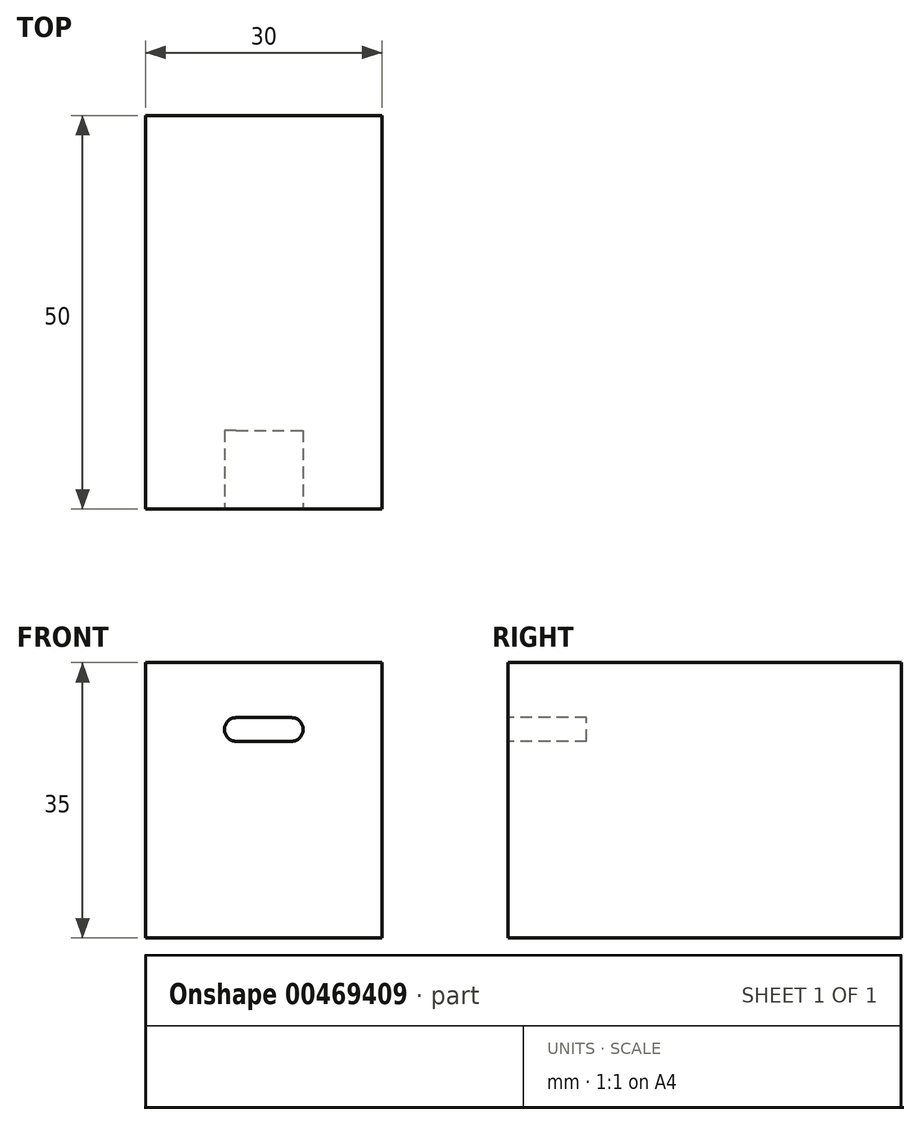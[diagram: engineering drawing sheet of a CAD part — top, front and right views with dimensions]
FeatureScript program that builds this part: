
annotation { "Feature Type Name" : "Feature", "Feature Type Description" : "" }
export const myFeature = defineFeature(function(context is Context, id is Id, definition is map)
    precondition{}
    {
        {
            var Q0;
            Q0=qCreatedBy(makeId("Top.planeOp"),FACE);
            var sketch = newSketch(context, id + "F0", { "sketchPlane" : qUnion([Q0])});
            skLineSegment(sketch, "E0.bottom", {"start": v(15, -25) * mm, "end": v(-15, -25) * mm});
            skLineSegment(sketch, "E0.top", {"start": v(15, 25) * mm, "end": v(-15, 25) * mm});
            skLineSegment(sketch, "E0.left", {"start": v(15, -25) * mm, "end": v(15, 25) * mm});
            skLineSegment(sketch, "E0.right", {"start": v(-15, -25) * mm, "end": v(-15, 25) * mm});
            skPoint(sketch, "E0.middle", {"position": v(0, 0) * mm});
            skSolve(sketch);
        }
        {
            var Q0;
            Q0 = qSketchRegion(id + "F0", true);
            extrude(context, id + "F1", {"entities" : qUnion([Q0]), "depth" : 35 * mm});
        }
        {
            var Q0;
            Q0=makeQuery(id+"F1.opExtrude","SWEPT_FACE",FACE,{"disambiguationData":[OSD([sQuery(id+"F0.wireOp",EDGE,"E0.bottom")])]});
            var sketch = newSketch(context, id + "F2", { "sketchPlane" : qUnion([Q0])});
            skLineSegment(sketch, "E1", {"start": v(0, 25) * mm, "end": v(3.5, 25) * mm});
            skLineSegment(sketch, "E2", {"start": v(0, 25) * mm, "end": v(-3.5, 25) * mm});
            skLineSegment(sketch, "E3", {"start": v(0, 28) * mm, "end": v(3.5, 28) * mm});
            skLineSegment(sketch, "E4", {"start": v(0, 28) * mm, "end": v(-3.5, 28) * mm});
            skArc(sketch, "E5", {"start": v(3.5, 25) * mm, "mid": v(5, 26.5) * mm, "end": v(3.5, 28) * mm});
            skArc(sketch, "E6", {"start": v(-3.5, 28) * mm, "mid": v(-5, 26.5) * mm, "end": v(-3.5, 25) * mm});
            skSolve(sketch);
        }
        {
            var Q0;
            Q0=makeQuery(id+"F2.imprint","IMPRINT",FACE,{"disambiguationData":[TD([[makeQuery(id+"F2.imprint","IMPRINT",EDGE,{"derivedFrom":sQuery(id+"F2.wireOp",EDGE,"E1")}),1.0]])]});
            extrude(context, id + "F3", {"entities" : qUnion([Q0]), "operationType" : NewBodyOperationType.REMOVE, "oppositeDirection" : true, "depth" : 10 * mm});
        }
    });
